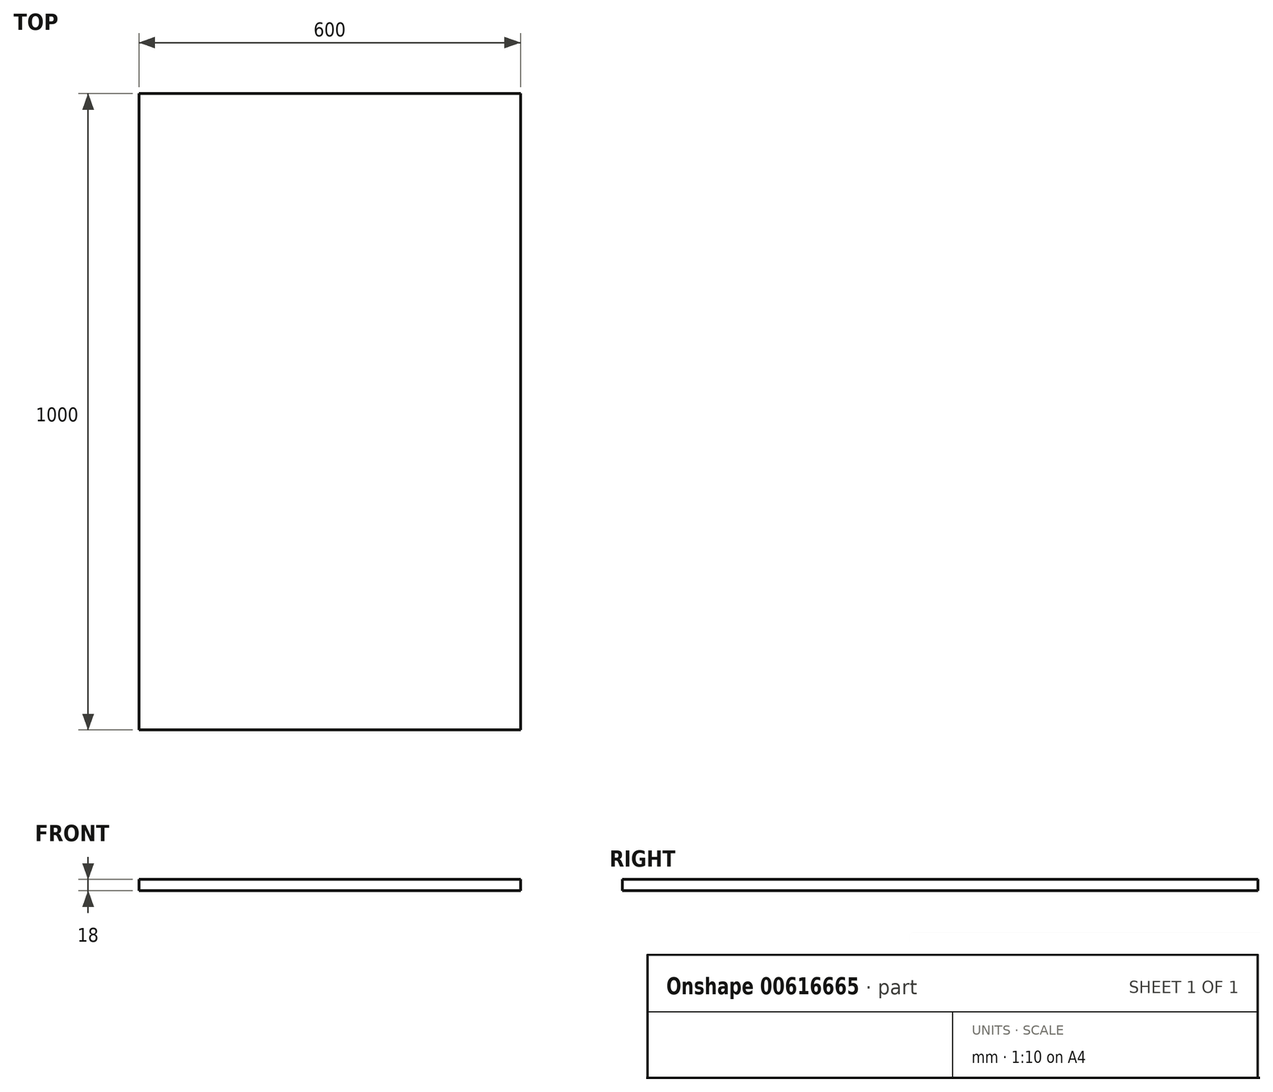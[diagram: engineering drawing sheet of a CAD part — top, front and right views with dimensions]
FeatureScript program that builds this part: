
annotation { "Feature Type Name" : "Feature", "Feature Type Description" : "" }
export const myFeature = defineFeature(function(context is Context, id is Id, definition is map)
    precondition{}
    {
        {
            var Q0;
            Q0=qCreatedBy(makeId("Top.planeOp"),FACE);
            var sketch = newSketch(context, id + "F0", { "sketchPlane" : qUnion([Q0])});
            skLineSegment(sketch, "E0.bottom", {"start": v(0, 0) * mm, "end": v(600, 0) * mm});
            skLineSegment(sketch, "E0.top", {"start": v(0, 1000) * mm, "end": v(600, 1000) * mm});
            skLineSegment(sketch, "E0.left", {"start": v(0, 0) * mm, "end": v(0, 1000) * mm});
            skLineSegment(sketch, "E0.right", {"start": v(600, 0) * mm, "end": v(600, 1000) * mm});
            skSolve(sketch);
        }
        {
            var Q0;
            Q0=makeQuery(id+"F0.imprint","IMPRINT",FACE,{"disambiguationData":[TD([[makeQuery(id+"F0.imprint","IMPRINT",EDGE,{"derivedFrom":sQuery(id+"F0.wireOp",EDGE,"E0.bottom")}),1.0]])]});
            extrude(context, id + "F1", {"entities" : qUnion([Q0]), "depth" : 18 * mm, "offsetDistance" : 25 * mm});
        }
    });
